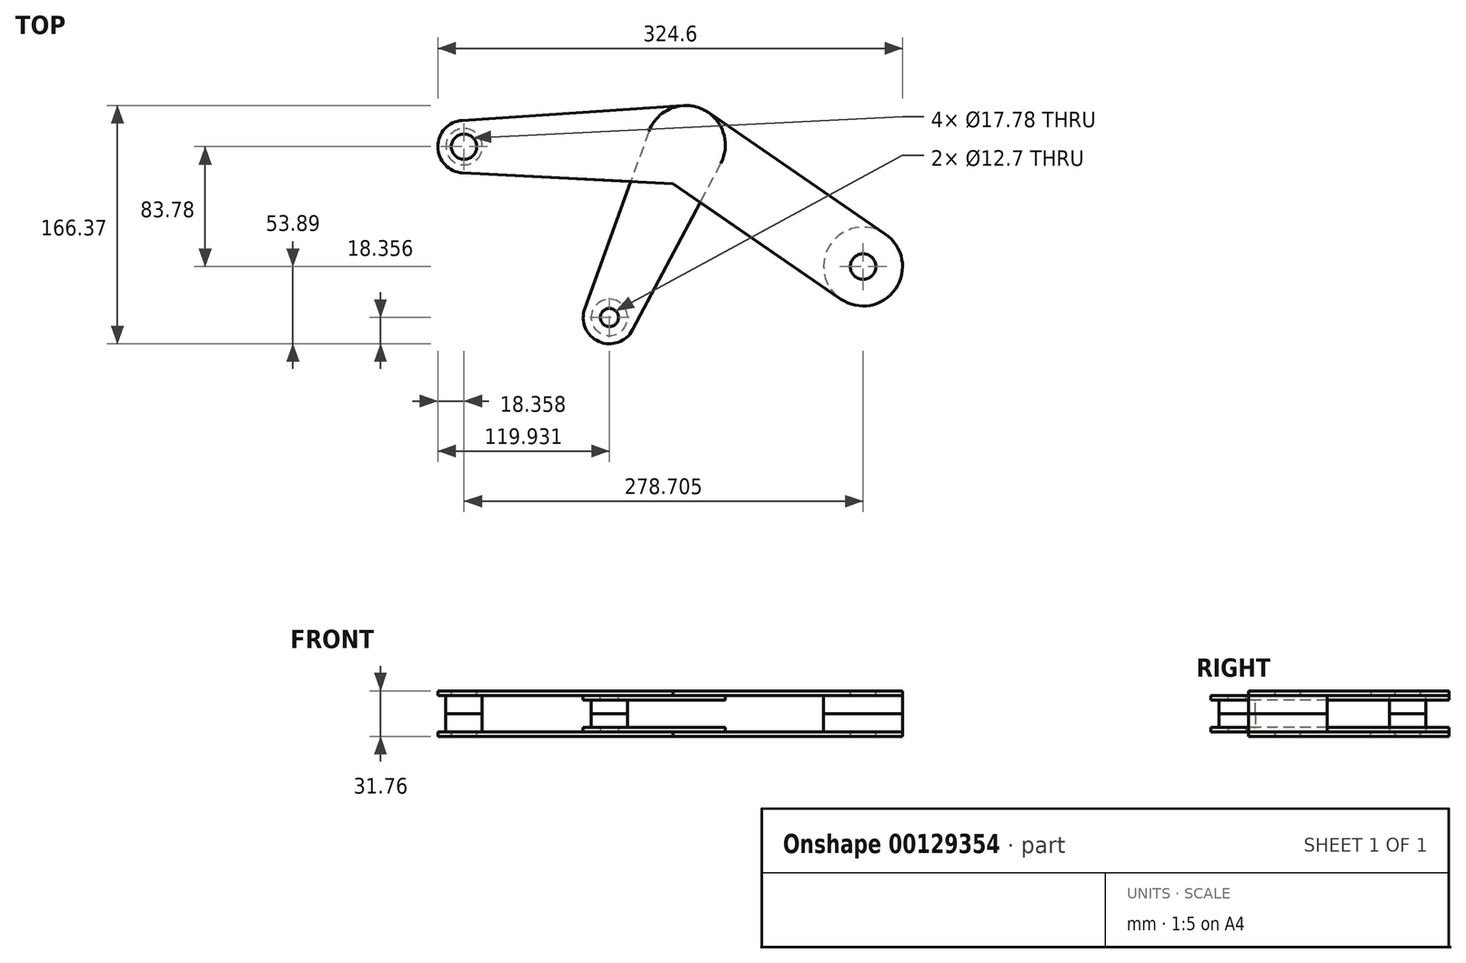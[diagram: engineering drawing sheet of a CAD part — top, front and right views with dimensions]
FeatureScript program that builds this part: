
annotation { "Feature Type Name" : "Feature", "Feature Type Description" : "" }
export const myFeature = defineFeature(function(context is Context, id is Id, definition is map)
    precondition{}
    {
        {
            var Q0;
            Q0=qCreatedBy(makeId("Top.planeOp"),FACE);
            var sketch = newSketch(context, id + "F0", { "sketchPlane" : qUnion([Q0])});
            skCircle(sketch, "E0", {"center": v(17.56, 55.78) * mm, "radius": 27.54 * mm});
            skCircle(sketch, "E1", {"center": v(-137.41, 54.6) * mm, "radius": 18.36 * mm});
            skLineSegment(sketch, "E2", {"start": v(-138.64, 72.93) * mm, "end": v(15.72, 83.25) * mm});
            skCircle(sketch, "E3", {"center": v(141.3, -29.17) * mm, "radius": 27.54 * mm});
            skLineSegment(sketch, "E4", {"start": v(33.15, 78.48) * mm, "end": v(156.88, -6.47) * mm});
            skCircle(sketch, "E5", {"center": v(-35.84, -64.7) * mm, "radius": 18.36 * mm});
            skLineSegment(sketch, "E6", {"start": v(-8.33, 65.15) * mm, "end": v(-53.1, -58.45) * mm});
            skLineSegment(sketch, "E7", {"start": v(41.9, 42.9) * mm, "end": v(-19.62, -73.3) * mm});
            skLineSegment(sketch, "E8", {"start": v(125.7, -51.87) * mm, "end": v(1.98, 33.07) * mm});
            skLineSegment(sketch, "E9", {"start": v(16.14, 28.28) * mm, "end": v(-138.36, 36.28) * mm});
            skCircle(sketch, "E10", {"center": v(-137.41, 54.6) * mm, "radius": 8.9 * mm});
            skCircle(sketch, "E11", {"center": v(141.3, -29.17) * mm, "radius": 8.9 * mm});
            skCircle(sketch, "E12", {"center": v(-35.84, -64.7) * mm, "radius": 6.35 * mm});
            skSolve(sketch);
        }
        {
            var Q0;
            {var subQ0=sQuery(id+"F0.wireOp",EDGE,"E1");var subQ1=makeQuery(id+"F0.imprint","INTERSECT",VERTEX,{"derivedFrom":[subQ0,sQuery(id+"F0.wireOp",EDGE,"E2")]});Q0=makeQuery(id+"F0.imprint","IMPRINT",FACE,{"disambiguationData":[TD([[makeQuery(id+"F0.imprint","IMPRINT",EDGE,{"disambiguationData":[TD([[subQ1,-1.0]])],"derivedFrom":subQ0}),1.0]])]});}
            var Q1;
            {var subQ0=sQuery(id+"F0.wireOp",EDGE,"E3");var subQ1=makeQuery(id+"F0.imprint","INTERSECT",VERTEX,{"derivedFrom":[subQ0,sQuery(id+"F0.wireOp",EDGE,"E4")]});Q1=makeQuery(id+"F0.imprint","IMPRINT",FACE,{"disambiguationData":[TD([[makeQuery(id+"F0.imprint","IMPRINT",EDGE,{"disambiguationData":[TD([[subQ1,-1.0]])],"derivedFrom":subQ0}),1.0]])]});}
            var Q2;
            {var subQ5=sQuery(id+"F0.wireOp",EDGE,"E2");Q2=makeQuery(id+"F0.imprint","IMPRINT",FACE,{"disambiguationData":[TD([[makeQuery(id+"F0.imprint","IMPRINT",EDGE,{"derivedFrom":subQ5}),-1.0]])]});}
            var Q3;
            {var subQ5=sQuery(id+"F0.wireOp",EDGE,"E4");Q3=makeQuery(id+"F0.imprint","IMPRINT",FACE,{"disambiguationData":[TD([[makeQuery(id+"F0.imprint","IMPRINT",EDGE,{"derivedFrom":subQ5}),-1.0]])]});}
            var Q4;
            {var subQ0=sQuery(id+"F0.wireOp",EDGE,"E6");var subQ1=sQuery(id+"F0.wireOp",EDGE,"E0");var subQ2=makeQuery(id+"F0.imprint","INTERSECT",VERTEX,{"derivedFrom":[subQ1,subQ0]});Q4=makeQuery(id+"F0.imprint","IMPRINT",FACE,{"disambiguationData":[TD([[makeQuery(id+"F0.imprint","IMPRINT",EDGE,{"disambiguationData":[TD([[subQ2,-1.0]])],"derivedFrom":subQ1}),-1.0]])]});}
            var Q5;
            {var subQ0=sQuery(id+"F0.wireOp",EDGE,"E7");var subQ1=sQuery(id+"F0.wireOp",EDGE,"E0");var subQ2=makeQuery(id+"F0.imprint","INTERSECT",VERTEX,{"derivedFrom":[subQ1,subQ0]});Q5=makeQuery(id+"F0.imprint","IMPRINT",FACE,{"disambiguationData":[TD([[makeQuery(id+"F0.imprint","IMPRINT",EDGE,{"disambiguationData":[TD([[subQ2,1.0]])],"derivedFrom":subQ1}),-1.0]])]});}
            var Q6;
            {var subQ0=sQuery(id+"F0.wireOp",EDGE,"E0");var subQ4=makeQuery(id+"F0.imprint","INTERSECT",VERTEX,{"derivedFrom":[subQ0,sQuery(id+"F0.wireOp",EDGE,"E2")]});Q6=makeQuery(id+"F0.imprint","IMPRINT",FACE,{"disambiguationData":[TD([[makeQuery(id+"F0.imprint","IMPRINT",EDGE,{"disambiguationData":[TD([[subQ4,1.0]])],"derivedFrom":subQ0}),1.0]])]});}
            var Q7;
            {var subQ0=sQuery(id+"F0.wireOp",EDGE,"E8");var subQ1=sQuery(id+"F0.wireOp",EDGE,"E0");var subQ2=makeQuery(id+"F0.imprint","INTERSECT",VERTEX,{"derivedFrom":[subQ1,subQ0]});Q7=makeQuery(id+"F0.imprint","IMPRINT",FACE,{"disambiguationData":[TD([[makeQuery(id+"F0.imprint","IMPRINT",EDGE,{"disambiguationData":[TD([[subQ2,-1.0]])],"derivedFrom":subQ1}),-1.0]])]});}
            extrude(context, id + "F1", {"entities" : qUnion([Q0, Q1, Q2, Q3, Q4, Q5, Q6, Q7]), "depth" : 3.17 * mm});
        }
        {
            var Q0;
            {var subQ0=sQuery(id+"F0.wireOp",EDGE,"E5");var subQ1=makeQuery(id+"F0.imprint","INTERSECT",VERTEX,{"derivedFrom":[subQ0,sQuery(id+"F0.wireOp",EDGE,"E6")]});Q0=makeQuery(id+"F0.imprint","IMPRINT",FACE,{"disambiguationData":[TD([[makeQuery(id+"F0.imprint","IMPRINT",EDGE,{"disambiguationData":[TD([[subQ1,-1.0]])],"derivedFrom":subQ0}),1.0]])]});}
            var Q1;
            {var subQ5=sQuery(id+"F0.wireOp",EDGE,"E5");var subQ7=sQuery(id+"F0.wireOp",EDGE,"E6");var subQ8=makeQuery(id+"F0.imprint","INTERSECT",VERTEX,{"derivedFrom":[subQ5,subQ7]});Q1=makeQuery(id+"F0.imprint","IMPRINT",FACE,{"disambiguationData":[TD([[makeQuery(id+"F0.imprint","IMPRINT",EDGE,{"disambiguationData":[TD([[subQ8,1.0]])],"derivedFrom":subQ5}),-1.0]])]});}
            var Q2;
            {var subQ0=sQuery(id+"F0.wireOp",EDGE,"E7");var subQ1=sQuery(id+"F0.wireOp",EDGE,"E0");var subQ2=makeQuery(id+"F0.imprint","INTERSECT",VERTEX,{"derivedFrom":[subQ1,subQ0]});Q2=makeQuery(id+"F0.imprint","IMPRINT",FACE,{"disambiguationData":[TD([[makeQuery(id+"F0.imprint","IMPRINT",EDGE,{"disambiguationData":[TD([[subQ2,1.0]])],"derivedFrom":subQ1}),-1.0]])]});}
            var Q3;
            {var subQ0=sQuery(id+"F0.wireOp",EDGE,"E0");var subQ4=makeQuery(id+"F0.imprint","INTERSECT",VERTEX,{"derivedFrom":[subQ0,sQuery(id+"F0.wireOp",EDGE,"E2")]});Q3=makeQuery(id+"F0.imprint","IMPRINT",FACE,{"disambiguationData":[TD([[makeQuery(id+"F0.imprint","IMPRINT",EDGE,{"disambiguationData":[TD([[subQ4,1.0]])],"derivedFrom":subQ0}),1.0]])]});}
            var Q4;
            {var subQ0=sQuery(id+"F0.wireOp",EDGE,"E6");var subQ1=sQuery(id+"F0.wireOp",EDGE,"E0");var subQ2=makeQuery(id+"F0.imprint","INTERSECT",VERTEX,{"derivedFrom":[subQ1,subQ0]});Q4=makeQuery(id+"F0.imprint","IMPRINT",FACE,{"disambiguationData":[TD([[makeQuery(id+"F0.imprint","IMPRINT",EDGE,{"disambiguationData":[TD([[subQ2,-1.0]])],"derivedFrom":subQ1}),-1.0]])]});}
            var Q5;
            {var subQ0=sQuery(id+"F0.wireOp",EDGE,"E8");var subQ1=sQuery(id+"F0.wireOp",EDGE,"E0");var subQ2=makeQuery(id+"F0.imprint","INTERSECT",VERTEX,{"derivedFrom":[subQ1,subQ0]});Q5=makeQuery(id+"F0.imprint","IMPRINT",FACE,{"disambiguationData":[TD([[makeQuery(id+"F0.imprint","IMPRINT",EDGE,{"disambiguationData":[TD([[subQ2,-1.0]])],"derivedFrom":subQ1}),-1.0]])]});}
            extrude(context, id + "F2", {"entities" : qUnion([Q0, Q1, Q2, Q3, Q4, Q5]), "oppositeDirection" : true, "depth" : 3.17 * mm});
        }
        {
            var Q0;
            Q0=qCreatedBy(makeId("Top.planeOp"),FACE);
            cPlane(context, id + "F3", {"entities" : qUnion([Q0]), "cplaneType" : CPlaneType.OFFSET, "offset" : 12.7 * mm, "oppositeDirection" : true, "width" : 152.4 * mm, "height" : 152.4 * mm});
        }
        {
            var Q0;
            Q0=makeQuery(id+"F1.opExtrude","CAP_FACE",FACE,{"disambiguationData":[OSD([sQuery(id+"F0.wireOp",EDGE,"E0"),sQuery(id+"F0.wireOp",EDGE,"E1"),sQuery(id+"F0.wireOp",EDGE,"E2"),sQuery(id+"F0.wireOp",EDGE,"E3"),sQuery(id+"F0.wireOp",EDGE,"E4"),sQuery(id+"F0.wireOp",EDGE,"E8"),sQuery(id+"F0.wireOp",EDGE,"E9"),sQuery(id+"F0.wireOp",EDGE,"E10"),sQuery(id+"F0.wireOp",EDGE,"E11")])],"isStart":false});
            var sketch = newSketch(context, id + "F4", { "sketchPlane" : qUnion([Q0])});
            skCircle(sketch, "E13", {"center": v(141.3, -29.17) * mm, "radius": 27.54 * mm});
            skCircle(sketch, "E14", {"center": v(-137.41, 54.6) * mm, "radius": 12.7 * mm});
            skSolve(sketch);
        }
        {
            var Q0;
            Q0=makeQuery(id+"F2.opExtrude","CAP_FACE",FACE,{"disambiguationData":[OSD([sQuery(id+"F0.wireOp",EDGE,"E0"),sQuery(id+"F0.wireOp",EDGE,"E5"),sQuery(id+"F0.wireOp",EDGE,"E6"),sQuery(id+"F0.wireOp",EDGE,"E7"),sQuery(id+"F0.wireOp",EDGE,"E12")])],"isStart":true});
            var sketch = newSketch(context, id + "F5", { "sketchPlane" : qUnion([Q0])});
            skCircle(sketch, "E15", {"center": v(-35.84, -64.7) * mm, "radius": 12.7 * mm});
            skSolve(sketch);
        }
        {
            var Q0;
            Q0 = qSketchRegion(id + "F4", true);
            var Q1;
            Q1 = qSketchRegion(id + "F5", true);
            var Q2;
            Q2=qCreatedBy(id+"F3.planeOp",FACE);
            extrude(context, id + "F6", {"entities" : qUnion([Q0, Q1]), "endBound" : BoundingType.UP_TO_SURFACE, "oppositeDirection" : true, "endBoundEntityFace" : qUnion([Q2]), "depth" : 25.4 * mm});
        }
        {
            var Q0;
            Q0=makeQuery(id+"F1.opExtrude","SWEPT_BODY",BODY,{"disambiguationData":[OSD([sQuery(id+"F0.wireOp",EDGE,"E0"),sQuery(id+"F0.wireOp",EDGE,"E1"),sQuery(id+"F0.wireOp",EDGE,"E2"),sQuery(id+"F0.wireOp",EDGE,"E3"),sQuery(id+"F0.wireOp",EDGE,"E4"),sQuery(id+"F0.wireOp",EDGE,"E8"),sQuery(id+"F0.wireOp",EDGE,"E9"),sQuery(id+"F0.wireOp",EDGE,"E10"),sQuery(id+"F0.wireOp",EDGE,"E11")])]});
            var Q1;
            Q1=makeQuery(id+"F2.opExtrude","SWEPT_BODY",BODY,{"disambiguationData":[OSD([sQuery(id+"F0.wireOp",EDGE,"E0"),sQuery(id+"F0.wireOp",EDGE,"E5"),sQuery(id+"F0.wireOp",EDGE,"E6"),sQuery(id+"F0.wireOp",EDGE,"E7"),sQuery(id+"F0.wireOp",EDGE,"E12")])]});
            var Q2;
            Q2=makeQuery(id+"F6.opExtrude","SWEPT_BODY",BODY,{"disambiguationData":[OSD([sQuery(id+"F4.wireOp",EDGE,"E13")])]});
            var Q3;
            Q3=makeQuery(id+"F6.opExtrude","SWEPT_BODY",BODY,{"disambiguationData":[OSD([sQuery(id+"F4.wireOp",EDGE,"E14")])]});
            var Q4;
            Q4=makeQuery(id+"F6.opExtrude","SWEPT_BODY",BODY,{"disambiguationData":[OSD([sQuery(id+"F5.wireOp",EDGE,"E15")])]});
            booleanBodies(context, id + "F7", {"operationType" : BooleanOperationType.SUBTRACTION, "tools" : qUnion([Q0, Q1]), "targets" : qUnion([Q2, Q3, Q4]), "keepTools" : true});
        }
        {
            var Q0;
            Q0=makeQuery(id+"F6.opExtrude","CAP_FACE",FACE,{"disambiguationData":[OSD([sQuery(id+"F4.wireOp",EDGE,"E14")])],"isStart":true});
            var Q1;
            Q1=makeQuery(id+"F7.opBoolean","COPY",EDGE,{"derivedFrom":makeQuery(id+"F2.opExtrude","CAP_EDGE",EDGE,{"disambiguationData":[OSD([sQuery(id+"F0.wireOp",EDGE,"E12")])],"isStart":true})});
            var Q2;
            Q2=makeQuery(id+"F6.opExtrude","CAP_FACE",FACE,{"disambiguationData":[OSD([sQuery(id+"F4.wireOp",EDGE,"E13")])],"isStart":true});
            fillet(context, id + "F8", {"entities" : qUnion([Q0, Q1, Q2]), "radius" : 2.03 * mm, "tangentPropagation" : true, "allowEdgeOverflow" : false});
        }
        {
            var Q0;
            Q0=makeQuery(id+"F6.opExtrude","SWEPT_BODY",BODY,{"disambiguationData":[OSD([sQuery(id+"F4.wireOp",EDGE,"E13")])]});
            var Q1;
            Q1=makeQuery(id+"F6.opExtrude","SWEPT_BODY",BODY,{"disambiguationData":[OSD([sQuery(id+"F4.wireOp",EDGE,"E14")])]});
            var Q2;
            Q2=makeQuery(id+"F6.opExtrude","SWEPT_BODY",BODY,{"disambiguationData":[OSD([sQuery(id+"F5.wireOp",EDGE,"E15")])]});
            var Q3;
            Q3=qCreatedBy(id+"F3.planeOp",FACE);
            mirror(context, id + "F9", {"entities" : qUnion([Q0, Q1, Q2]), "mirrorPlane" : qUnion([Q3])});
        }
        {
            var Q0;
            Q0=makeQuery(id+"F1.opExtrude","SWEPT_BODY",BODY,{"disambiguationData":[OSD([sQuery(id+"F0.wireOp",EDGE,"E0"),sQuery(id+"F0.wireOp",EDGE,"E1"),sQuery(id+"F0.wireOp",EDGE,"E2"),sQuery(id+"F0.wireOp",EDGE,"E3"),sQuery(id+"F0.wireOp",EDGE,"E4"),sQuery(id+"F0.wireOp",EDGE,"E8"),sQuery(id+"F0.wireOp",EDGE,"E9"),sQuery(id+"F0.wireOp",EDGE,"E10"),sQuery(id+"F0.wireOp",EDGE,"E11")])]});
            var Q1;
            Q1=makeQuery(id+"F2.opExtrude","SWEPT_BODY",BODY,{"disambiguationData":[OSD([sQuery(id+"F0.wireOp",EDGE,"E0"),sQuery(id+"F0.wireOp",EDGE,"E5"),sQuery(id+"F0.wireOp",EDGE,"E6"),sQuery(id+"F0.wireOp",EDGE,"E7"),sQuery(id+"F0.wireOp",EDGE,"E12")])]});
            var Q2;
            Q2=qCreatedBy(id+"F3.planeOp",FACE);
            mirror(context, id + "F10", {"entities" : qUnion([Q0, Q1]), "mirrorPlane" : qUnion([Q2])});
        }
    });
